# Revit family: G90.205.xxx_with standard interieur
name_source: partatom
category: Möbelsysteme
revit_build: Autodesk Revit 2015 (Build: 20160512_1515(x64)
units: mm (PartAtom-declared; Revit-internal decimal feet)

## types (18) — shared parameters
Beschreibung = GS-tested safety storage cabinets for unrestricted storage of flammable hazardous materials in work areas in accordance with EN 14470-1 and TRGS 510 with a fire resistance of 90 (Type 90)
Cabinet depth = 616 mm
Diff. pressure (Air change 10 times) = 5.0 Pa
Hersteller = asecos GmbH
Price information = Price from fall 2017
Price information 2 = Prices are ex works and without taxes and shipping
Product video = https://www.youtube.com
Typenbild = <Keine Auswahl>
URL = https://www.asecos.com

## per-type parameters (varying)
- G90.205.140, standard interior, pure white: 1200 mm cabinet=Nein; 1400 mm cabinet=Ja; 600 mm / 1450 mm=Nein; 600 mm / 2050 mm=Nein; 600 mm 2F=Nein; 600 mm cabinet=Nein; 900 mm cabinet=Nein; Air change 10 times=2.5 L/s; Air change 120 times=30.8 L/s; Air duct distance=584 mm  [stored 1.91601 ft]; Bestellnummer DACH=30641-005-30642; Cabinet colour=RAL 9010 Pure white; Cabinet height=2050 mm  [stored 6.72572 ft]; Cabinet width=1398 mm; Diff. pressure (Air change 120 times EK5/AK4)=143.0 Pa; Distributed load=5.60 kN/m²; Door colour=RAL 9010 Pure white; Door width=654 mm; Double door=Ja; Handle position=764 mm; High Cabinet=Ja; Inner body width=40 mm  [stored 0.131234 ft]; Kosten=3792 $; Low Cabinet=Nein; Modell=G90.205.140 with standard interior; Order No. Global=30641-005-30642; Single door=Nein; Sticker position lh=1831 mm; Sticker position ls=913 mm; Sticker position rb=219 mm
- G90.205.140, standard interior, light grey: 1200 mm cabinet=Nein; 1400 mm cabinet=Ja; 600 mm / 1450 mm=Nein; 600 mm / 2050 mm=Nein; 600 mm 2F=Nein; 600 mm cabinet=Nein; 900 mm cabinet=Nein; Air change 10 times=2.5 L/s; Air change 120 times=30.8 L/s; Air duct distance=584 mm  [stored 1.91601 ft]; Bestellnummer DACH=30641-001-30642; Cabinet colour=RAL 7035 Light grey; Cabinet height=2050 mm  [stored 6.72572 ft]; Cabinet width=1398 mm; Diff. pressure (Air change 120 times EK5/AK4)=143.0 Pa; Distributed load=5.60 kN/m²; Door colour=RAL 7035 Light grey; Door width=654 mm; Double door=Ja; Handle position=764 mm; High Cabinet=Ja; Inner body width=40 mm  [stored 0.131234 ft]; Kosten=3792 $; Low Cabinet=Nein; Modell=G90.205.140 with standard interior; Order No. Global=30641-001-30642; Single door=Nein; Sticker position lh=1831 mm; Sticker position ls=913 mm; Sticker position rb=219 mm
- G90.205.140, standard interior, warning yellow: 1200 mm cabinet=Nein; 1400 mm cabinet=Ja; 600 mm / 1450 mm=Nein; 600 mm / 2050 mm=Nein; 600 mm 2F=Nein; 600 mm cabinet=Nein; 900 mm cabinet=Nein; Air change 10 times=2.5 L/s; Air change 120 times=30.8 L/s; Air duct distance=584 mm  [stored 1.91601 ft]; Bestellnummer DACH=30641-002-30642; Cabinet colour=RAL 1004 warning yellow; Cabinet height=2050 mm  [stored 6.72572 ft]; Cabinet width=1398 mm; Diff. pressure (Air change 120 times EK5/AK4)=143.0 Pa; Distributed load=5.60 kN/m²; Door colour=RAL 1004 warning yellow; Door width=654 mm; Double door=Ja; Handle position=764 mm; High Cabinet=Ja; Inner body width=40 mm  [stored 0.131234 ft]; Kosten=3792 $; Low Cabinet=Nein; Modell=G90.205.140 with standard interior; Order No. Global=30641-002-30642; Single door=Nein; Sticker position lh=1831 mm; Sticker position ls=913 mm; Sticker position rb=219 mm
- G90.205.120, standard interior, pure white: 1200 mm cabinet=Ja; 1400 mm cabinet=Nein; 600 mm / 1450 mm=Nein; 600 mm / 2050 mm=Nein; 600 mm 2F=Nein; 600 mm cabinet=Nein; 900 mm cabinet=Nein; Air change 10 times=2.2 L/s; Air change 120 times=25.8 L/s; Air duct distance=484 mm  [stored 1.58793 ft]; Bestellnummer DACH=30657-005-30658; Cabinet colour=RAL 9010 Pure white; Cabinet height=2050 mm  [stored 6.72572 ft]; Cabinet width=1198 mm; Diff. pressure (Air change 120 times EK5/AK4)=103.0 Pa; Distributed load=6.13 kN/m²; Door colour=RAL 9010 Pure white; Door width=554 mm  [stored 1.81759 ft]; Double door=Ja; Handle position=664 mm; High Cabinet=Ja; Inner body width=40 mm  [stored 0.131234 ft]; Kosten=3330 $; Low Cabinet=Nein; Modell=G90.205.120 with standard interior; Order No. Global=30657-005-30658; Single door=Nein; Sticker position lh=1831 mm; Sticker position ls=813 mm; Sticker position rb=219 mm
- G90.205.120, standard interior, light grey: 1200 mm cabinet=Ja; 1400 mm cabinet=Nein; 600 mm / 1450 mm=Nein; 600 mm / 2050 mm=Nein; 600 mm 2F=Nein; 600 mm cabinet=Nein; 900 mm cabinet=Nein; Air change 10 times=2.2 L/s; Air change 120 times=25.8 L/s; Air duct distance=484 mm  [stored 1.58793 ft]; Bestellnummer DACH=30657-001-30658; Cabinet colour=RAL 7035 Light grey; Cabinet height=2050 mm  [stored 6.72572 ft]; Cabinet width=1198 mm; Diff. pressure (Air change 120 times EK5/AK4)=103.0 Pa; Distributed load=6.13 kN/m²; Door colour=RAL 7035 Light grey; Door width=554 mm  [stored 1.81759 ft]; Double door=Ja; Handle position=664 mm; High Cabinet=Ja; Inner body width=40 mm  [stored 0.131234 ft]; Kosten=3330 $; Low Cabinet=Nein; Modell=G90.205.120 with standard interior; Order No. Global=30657-001-30658; Single door=Nein; Sticker position lh=1831 mm; Sticker position ls=813 mm; Sticker position rb=219 mm
- G90.205.120, standard interior, warning yellow: 1200 mm cabinet=Ja; 1400 mm cabinet=Nein; 600 mm / 1450 mm=Nein; 600 mm / 2050 mm=Nein; 600 mm 2F=Nein; 600 mm cabinet=Nein; 900 mm cabinet=Nein; Air change 10 times=2.2 L/s; Air change 120 times=25.8 L/s; Air duct distance=484 mm  [stored 1.58793 ft]; Bestellnummer DACH=30657-002-30658; Cabinet colour=RAL 1004 warning yellow; Cabinet height=2050 mm  [stored 6.72572 ft]; Cabinet width=1199 mm; Diff. pressure (Air change 120 times EK5/AK4)=103.0 Pa; Distributed load=6.13 kN/m²; Door colour=RAL 1004 warning yellow; Door width=554 mm  [stored 1.81759 ft]; Double door=Ja; Handle position=664 mm; High Cabinet=Ja; Inner body width=40 mm  [stored 0.131234 ft]; Kosten=3330 $; Low Cabinet=Nein; Modell=G90.205.120 with standard interior; Order No. Global=30657-002-30658; Single door=Nein; Sticker position lh=1831 mm; Sticker position ls=813 mm; Sticker position rb=219 mm
- G90.205.090, standard interior, pure wite: 1200 mm cabinet=Nein; 1400 mm cabinet=Nein; 600 mm / 1450 mm=Nein; 600 mm / 2050 mm=Nein; 600 mm 2F=Nein; 600 mm cabinet=Nein; 900 mm cabinet=Ja; Air change 10 times=1.7 L/s; Air change 120 times=18.3 L/s; Air duct distance=334 mm  [stored 1.0958 ft]; Bestellnummer DACH=30667-005-30668; Cabinet colour=RAL 9010 Pure white; Cabinet height=2050 mm  [stored 6.72572 ft]; Cabinet width=898 mm; Diff. pressure (Air change 120 times EK5/AK4)=147.0 Pa; Distributed load=7.38 kN/m²; Door colour=RAL 9010 Pure white; Door width=404 mm  [stored 1.32546 ft]; Double door=Ja; Handle position=515 mm; High Cabinet=Ja; Inner body width=40 mm  [stored 0.131234 ft]; Kosten=3059 $; Low Cabinet=Nein; Modell=G90.205.090 with standard interior; Order No. Global=30667-005-30668; Single door=Nein; Sticker position lh=1831 mm; Sticker position ls=663 mm; Sticker position rb=219 mm
- G90.205.090, standard interior, light grey: 1200 mm cabinet=Nein; 1400 mm cabinet=Nein; 600 mm / 1450 mm=Nein; 600 mm / 2050 mm=Nein; 600 mm 2F=Nein; 600 mm cabinet=Nein; 900 mm cabinet=Ja; Air change 10 times=1.7 L/s; Air change 120 times=18.3 L/s; Air duct distance=334 mm  [stored 1.0958 ft]; Bestellnummer DACH=30667-001-30668; Cabinet colour=RAL 7035 Light grey; Cabinet height=2050 mm  [stored 6.72572 ft]; Cabinet width=898 mm; Diff. pressure (Air change 120 times EK5/AK4)=147.0 Pa; Distributed load=7.38 kN/m²; Door colour=RAL 7035 Light grey; Door width=404 mm  [stored 1.32546 ft]; Double door=Ja; Handle position=515 mm; High Cabinet=Ja; Inner body width=40 mm  [stored 0.131234 ft]; Kosten=3059 $; Low Cabinet=Nein; Modell=G90.205.090 with standard interior; Order No. Global=30667-001-30668; Single door=Nein; Sticker position lh=1831 mm; Sticker position ls=663 mm; Sticker position rb=219 mm
- G90.205.090, standard interior, warning yellow: 1200 mm cabinet=Nein; 1400 mm cabinet=Nein; 600 mm / 1450 mm=Nein; 600 mm / 2050 mm=Nein; 600 mm 2F=Nein; 600 mm cabinet=Nein; 900 mm cabinet=Ja; Air change 10 times=1.7 L/s; Air change 120 times=18.3 L/s; Air duct distance=334 mm  [stored 1.0958 ft]; Bestellnummer DACH=30667-002-30668; Cabinet colour=RAL 1004 warning yellow; Cabinet height=2050 mm  [stored 6.72572 ft]; Cabinet width=898 mm; Diff. pressure (Air change 120 times EK5/AK4)=147.0 Pa; Distributed load=7.38 kN/m²; Door colour=RAL 1004 warning yellow; Door width=404 mm  [stored 1.32546 ft]; Double door=Ja; Handle position=515 mm; High Cabinet=Ja; Inner body width=40 mm  [stored 0.131234 ft]; Kosten=3059 $; Low Cabinet=Nein; Modell=G90.205.090 with standard interior; Order No. Global=30667-002-30668; Single door=Nein; Sticker position lh=1831 mm; Sticker position ls=663 mm; Sticker position rb=219 mm
- G90.205.060.2F, standard interior, pure white: 1200 mm cabinet=Nein; 1400 mm cabinet=Nein; 600 mm / 1450 mm=Nein; 600 mm / 2050 mm=Nein; 600 mm 2F=Ja; 600 mm cabinet=Ja; 900 mm cabinet=Nein; Air change 10 times=1.1 L/s; Air change 120 times=12.5 L/s; Air duct distance=184 mm  [stored 0.603675 ft]; Bestellnummer DACH=30678-005-30682; Cabinet colour=RAL 9010 Pure white; Cabinet height=2050 mm  [stored 6.72572 ft]; Cabinet width=597 mm  [stored 1.95866 ft]; Diff. pressure (Air change 120 times EK5/AK4)=76.0 Pa; Distributed load=9.80 kN/m²; Door colour=RAL 9010 Pure white; Door width=514 mm  [stored 1.68635 ft]; Double door=Nein; Handle position=454 mm; High Cabinet=Ja; Inner body width=23 mm; Kosten=2993 $; Low Cabinet=Nein; Modell=G90.205.060.2F with standard interior; Order No. Global=30678-005-30682; Single door=Ja; Sticker position lh=2050 mm  [stored 6.72572 ft]; Sticker position ls=555 mm  [stored 1.82087 ft]; Sticker position rb=0 mm  [stored 0 ft]
- G90.205.060.2F, standard interior, light grey: 1200 mm cabinet=Nein; 1400 mm cabinet=Nein; 600 mm / 1450 mm=Nein; 600 mm / 2050 mm=Nein; 600 mm 2F=Ja; 600 mm cabinet=Ja; 900 mm cabinet=Nein; Air change 10 times=1.1 L/s; Air change 120 times=12.5 L/s; Air duct distance=184 mm  [stored 0.603675 ft]; Bestellnummer DACH=30678-001-30682; Cabinet colour=RAL 7035 Light grey; Cabinet height=2050 mm  [stored 6.72572 ft]; Cabinet width=597 mm  [stored 1.95866 ft]; Diff. pressure (Air change 120 times EK5/AK4)=76.0 Pa; Distributed load=9.80 kN/m²; Door colour=RAL 7035 Light grey; Door width=514 mm  [stored 1.68635 ft]; Double door=Nein; Handle position=454 mm; High Cabinet=Ja; Inner body width=23 mm; Kosten=2993 $; Low Cabinet=Nein; Modell=G90.205.060.2F with standard interior; Order No. Global=30678-001-30682; Single door=Ja; Sticker position lh=2050 mm  [stored 6.72572 ft]; Sticker position ls=555 mm  [stored 1.82087 ft]; Sticker position rb=0 mm  [stored 0 ft]
- G90.205.060.2F, standard interior, warning yellow: 1200 mm cabinet=Nein; 1400 mm cabinet=Nein; 600 mm / 1450 mm=Nein; 600 mm / 2050 mm=Nein; 600 mm 2F=Ja; 600 mm cabinet=Ja; 900 mm cabinet=Nein; Air change 10 times=1.1 L/s; Air change 120 times=12.5 L/s; Air duct distance=184 mm  [stored 0.603675 ft]; Bestellnummer DACH=30678-002-30682; Cabinet colour=RAL 1004 warning yellow; Cabinet height=2050 mm  [stored 6.72572 ft]; Cabinet width=597 mm  [stored 1.95866 ft]; Diff. pressure (Air change 120 times EK5/AK4)=76.0 Pa; Distributed load=9.80 kN/m²; Door colour=RAL 1004 warning yellow; Door width=514 mm  [stored 1.68635 ft]; Double door=Nein; Handle position=454 mm; High Cabinet=Ja; Inner body width=23 mm; Kosten=2993 $; Low Cabinet=Nein; Modell=G90.205.060.2F with standard interior; Order No. Global=30678-002-30682; Single door=Ja; Sticker position lh=2050 mm  [stored 6.72572 ft]; Sticker position ls=555 mm  [stored 1.82087 ft]; Sticker position rb=0 mm  [stored 0 ft]
- G90.205.060, standard interior, pure white: 1200 mm cabinet=Nein; 1400 mm cabinet=Nein; 600 mm / 1450 mm=Nein; 600 mm / 2050 mm=Ja; 600 mm 2F=Nein; 600 mm cabinet=Ja; 900 mm cabinet=Nein; Air change 10 times=1.1 L/s; Air change 120 times=11.7 L/s; Air duct distance=184 mm  [stored 0.603675 ft]; Bestellnummer DACH=30676-005-30680; Cabinet colour=RAL 9010 Pure white; Cabinet height=2050 mm  [stored 6.72572 ft]; Cabinet width=598 mm; Diff. pressure (Air change 120 times EK5/AK4)=85.0 Pa; Distributed load=9.80 kN/m²; Door colour=RAL 9010 Pure white; Door width=514 mm  [stored 1.68635 ft]; Double door=Nein; Handle position=454 mm; High Cabinet=Ja; Inner body width=40 mm  [stored 0.131234 ft]; Kosten=2571 $; Low Cabinet=Nein; Modell=G90.205.060 with standard interior; Order No. Global=30676-005-30680; Single door=Ja; Sticker position lh=2050 mm  [stored 6.72572 ft]; Sticker position ls=555 mm  [stored 1.82087 ft]; Sticker position rb=0 mm  [stored 0 ft]
- G90.205.060, standard interior, light grey: 1200 mm cabinet=Nein; 1400 mm cabinet=Nein; 600 mm / 1450 mm=Nein; 600 mm / 2050 mm=Ja; 600 mm 2F=Nein; 600 mm cabinet=Ja; 900 mm cabinet=Nein; Air change 10 times=1.1 L/s; Air change 120 times=11.7 L/s; Air duct distance=184 mm  [stored 0.603675 ft]; Bestellnummer DACH=30676-001-30680; Cabinet colour=RAL 7035 Light grey; Cabinet height=2050 mm  [stored 6.72572 ft]; Cabinet width=598 mm; Diff. pressure (Air change 120 times EK5/AK4)=85.0 Pa; Distributed load=9.80 kN/m²; Door colour=RAL 7035 Light grey; Door width=514 mm  [stored 1.68635 ft]; Double door=Nein; Handle position=454 mm; High Cabinet=Ja; Inner body width=40 mm  [stored 0.131234 ft]; Kosten=2571 $; Low Cabinet=Nein; Modell=G90.205.060 with standard interior; Order No. Global=30676-001-30680; Single door=Ja; Sticker position lh=2050 mm  [stored 6.72572 ft]; Sticker position ls=555 mm  [stored 1.82087 ft]; Sticker position rb=0 mm  [stored 0 ft]
- G90.205.060, standard interior, warning yellow: 1200 mm cabinet=Nein; 1400 mm cabinet=Nein; 600 mm / 1450 mm=Nein; 600 mm / 2050 mm=Ja; 600 mm 2F=Nein; 600 mm cabinet=Ja; 900 mm cabinet=Nein; Air change 10 times=1.1 L/s; Air change 120 times=11.7 L/s; Air duct distance=184 mm  [stored 0.603675 ft]; Bestellnummer DACH=30676-002-30680; Cabinet colour=RAL 1004 warning yellow; Cabinet height=2050 mm  [stored 6.72572 ft]; Cabinet width=598 mm; Diff. pressure (Air change 120 times EK5/AK4)=85.0 Pa; Distributed load=9.80 kN/m²; Door colour=RAL 1004 warning yellow; Door width=514 mm  [stored 1.68635 ft]; Double door=Nein; Handle position=454 mm; High Cabinet=Ja; Inner body width=40 mm  [stored 0.131234 ft]; Kosten=2571 $; Low Cabinet=Nein; Modell=G90.205.060 with standard interior; Order No. Global=30676-002-30680; Single door=Ja; Sticker position lh=2050 mm  [stored 6.72572 ft]; Sticker position ls=555 mm  [stored 1.82087 ft]; Sticker position rb=0 mm  [stored 0 ft]
- G90.145.060, standard interior, pure white: 1200 mm cabinet=Nein; 1400 mm cabinet=Nein; 600 mm / 1450 mm=Ja; 600 mm / 2050 mm=Nein; 600 mm 2F=Nein; 600 mm cabinet=Ja; 900 mm cabinet=Nein; Air change 10 times=0.6 L/s; Air change 120 times=7.8 L/s; Air duct distance=184 mm  [stored 0.603675 ft]; Bestellnummer DACH=30689-005-30691; Cabinet colour=RAL 9010 Pure white; Cabinet height=1452 mm; Cabinet width=598 mm; Diff. pressure (Air change 120 times EK5/AK4)=42.0 Pa; Distributed load=8.92 kN/m²; Door colour=RAL 9010 Pure white; Door width=514 mm  [stored 1.68635 ft]; Double door=Nein; Handle position=454 mm; High Cabinet=Nein; Inner body width=40 mm  [stored 0.131234 ft]; Kosten=2571 $; Low Cabinet=Ja; Modell=G90.145.060 with standard interior; Order No. Global=30689-005-30691; Single door=Ja; Sticker position lh=1452 mm; Sticker position ls=555 mm  [stored 1.82087 ft]; Sticker position rb=0 mm  [stored 0 ft]
- G90.145.060, standard interior, warning yellow: 1200 mm cabinet=Nein; 1400 mm cabinet=Nein; 600 mm / 1450 mm=Ja; 600 mm / 2050 mm=Nein; 600 mm 2F=Nein; 600 mm cabinet=Ja; 900 mm cabinet=Nein; Air change 10 times=0.6 L/s; Air change 120 times=7.8 L/s; Air duct distance=184 mm  [stored 0.603675 ft]; Bestellnummer DACH=30689-002-30691; Cabinet colour=RAL 1004 warning yellow; Cabinet height=1452 mm; Cabinet width=598 mm; Diff. pressure (Air change 120 times EK5/AK4)=42.0 Pa; Distributed load=8.92 kN/m²; Door colour=RAL 1004 warning yellow; Door width=514 mm  [stored 1.68635 ft]; Double door=Nein; Handle position=454 mm; High Cabinet=Nein; Inner body width=40 mm  [stored 0.131234 ft]; Kosten=2571 $; Low Cabinet=Ja; Modell=G90.145.060 with standard interior; Order No. Global=30689-002-30691; Single door=Ja; Sticker position lh=1452 mm; Sticker position ls=555 mm  [stored 1.82087 ft]; Sticker position rb=0 mm  [stored 0 ft]
- G90.145.060, standard interior, light grey: 1200 mm cabinet=Nein; 1400 mm cabinet=Nein; 600 mm / 1450 mm=Ja; 600 mm / 2050 mm=Nein; 600 mm 2F=Nein; 600 mm cabinet=Ja; 900 mm cabinet=Nein; Air change 10 times=0.6 L/s; Air change 120 times=7.8 L/s; Air duct distance=184 mm  [stored 0.603675 ft]; Bestellnummer DACH=30689-001-30691; Cabinet colour=RAL 7035 Light grey; Cabinet height=1452 mm; Cabinet width=598 mm; Diff. pressure (Air change 120 times EK5/AK4)=42.0 Pa; Distributed load=8.92 kN/m²; Door colour=RAL 7035 Light grey; Door width=514 mm  [stored 1.68635 ft]; Double door=Nein; Handle position=454 mm; High Cabinet=Nein; Inner body width=40 mm  [stored 0.131234 ft]; Kosten=2571 $; Low Cabinet=Ja; Modell=G90.145.060 with standard interior; Order No. Global=30689-001-30691; Single door=Ja; Sticker position lh=1452 mm; Sticker position ls=555 mm  [stored 1.82087 ft]; Sticker position rb=0 mm  [stored 0 ft]

note: [stored X ft] marks values corroborated as IEEE doubles in the binary element streams (Revit-internal decimal feet)
